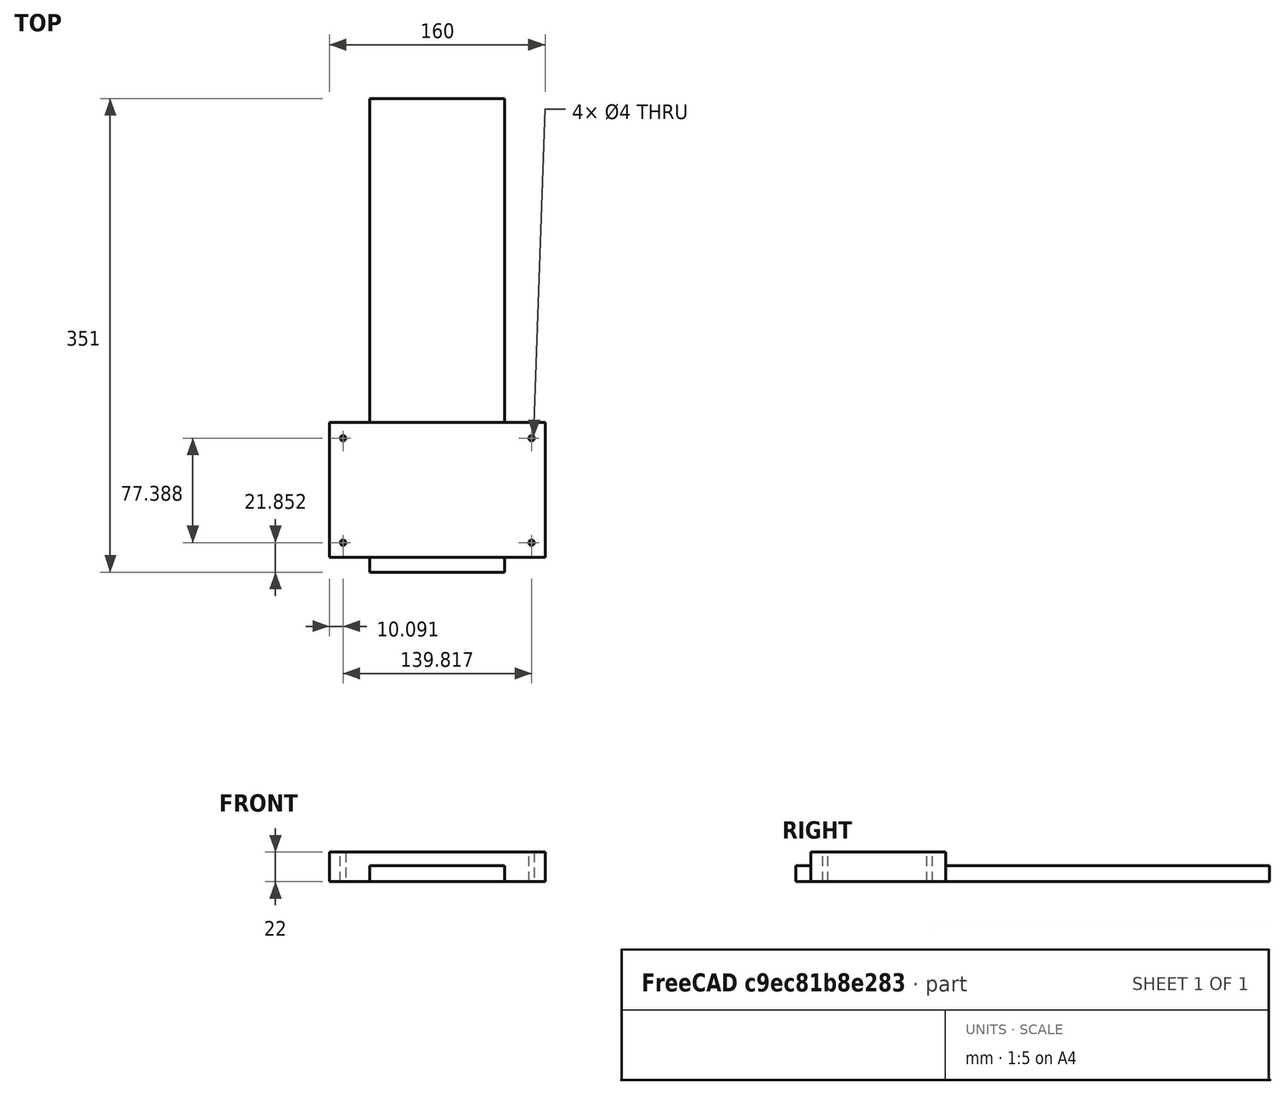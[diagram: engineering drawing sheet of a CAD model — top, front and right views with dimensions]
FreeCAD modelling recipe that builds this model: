
FCSTD DOCUMENT  (FreeCAD 0.20R29603 (Git))
Label: 100_Pedastil_Drawer
License: All rights reserved
LicenseURL: http://en.wikipedia.org/wiki/All_rights_reserved
objects: TechDraw::DrawViewDimension×6, Sketcher::SketchObject×3, TechDraw::DrawViewBalloon×3, PartDesign::Pad×2, TechDraw::DrawViewPart×2, Spreadsheet::Sheet×1, PartDesign::Pocket×1, PartDesign::Body×1, TechDraw::DrawSVGTemplate×1, TechDraw::DrawPage×1
note: 10 computed .brp shape members not serialized (recipe doc carries the construction recipe); baked Part::Feature solids carry a one-line shape summary decoded from their .brp

FEATURE [Spreadsheet::Sheet] Spreadsheet
  cells = B4=Drawer; C4=Value; D4=Nominal; E4=Var; F4=Description; G4=FILE
FEATURE [Sketcher::SketchObject] Sketch
  FullyConstrained = false
  MapMode = 5
  Support = -> [XY_Plane]
  sketch-geometry (14):
    g0: LineSegment StartX=-50 StartY=0 StartZ=0 EndX=-50 EndY=340 EndZ=0
    g1: LineSegment StartX=-50 StartY=340 StartZ=0 EndX=50 EndY=340 EndZ=0
    g2: LineSegment StartX=50 StartY=340 StartZ=0 EndX=50 EndY=0 EndZ=0
    g3: LineSegment StartX=50 StartY=100 StartZ=0 EndX=80 EndY=100 EndZ=0
    g4: LineSegment StartX=80 StartY=100 StartZ=0 EndX=80 EndY=0 EndZ=0
    g5: LineSegment StartX=80 StartY=0 StartZ=0 EndX=50 EndY=0 EndZ=0
    g6: LineSegment StartX=-50 StartY=100 StartZ=0 EndX=-80 EndY=100 EndZ=0
    g7: LineSegment StartX=-80 StartY=100 StartZ=0 EndX=-80 EndY=0 EndZ=0
    g8: LineSegment StartX=-80 StartY=0 StartZ=0 EndX=-50 EndY=0 EndZ=0
    g9: LineSegment StartX=-50 StartY=100 StartZ=0 EndX=-50 EndY=340 EndZ=0
    g10: LineSegment StartX=50 StartY=100 StartZ=0 EndX=50 EndY=340 EndZ=0
    g11: LineSegment StartX=50 StartY=0 StartZ=0 EndX=50 EndY=-11 EndZ=0
    g12: LineSegment StartX=50 StartY=-11 StartZ=0 EndX=-50 EndY=-11 EndZ=0
    g13: LineSegment StartX=-50 StartY=-11 StartZ=0 EndX=-50 EndY=0 EndZ=0
  constraints (38):
    c: PointOnObject(g0,g-1)
    c: Vertical(g0)
    c: Coincident(g1,g0)
    c: Horizontal(g1)
    c: Coincident(g2,g1)
    c: PointOnObject(g2,g-1)
    c: Vertical(g2)
    c: DistanceY(g2,g2) = 340
    c: DistanceX(g0,g2) = 100
    c: Coincident(g3,g4)
    c: Coincident(g4,g5)
    c: Horizontal(g3)
    c: Horizontal(g5)
    c: Vertical(g4)
    c: PointOnObject(g3,g2)
    c: PointOnObject(g4,g-1)
    c: Coincident(g6,g7)
    c: Coincident(g7,g8)
    c: Horizontal(g6)
    c: Horizontal(g8)
    c: Vertical(g7)
    c: PointOnObject(g6,g0)
    c: PointOnObject(g7,g-1)
    c: Equal(g4,g7)
    c: DistanceY(g4,g4) = 100
    c: DistanceX(g5,g5) = 30
    c: Equal(g5,g8)
    c: Coincident(g9,g6)
    c: Coincident(g9,g1)
    c: Coincident(g10,g3)
    c: Coincident(g10,g1)
    c: Coincident(g11,g12)
    c: Coincident(g12,g13)
    c: Horizontal(g12)
    c: Vertical(g11)
    c: Vertical(g13)
    c: DistanceY(g13,g13) = 11
    c: Coincident(g13,g8)
FEATURE [PartDesign::Pad] Pad
  Direction = (0,0,1)
  Length = 12
  Length2 = 10
  Profile = -> Sketch
  ReferenceAxis = -> Sketch [N_Axis]
  Type = 0
FEATURE [Sketcher::SketchObject] Sketch001
  ExternalGeometry = -> [Pad]
  FullyConstrained = true
  MapMode = 5
  Placement = pos=(0,0,12) rot=(0,0,1;0rad)
  Support = -> [Pad]
  sketch-geometry (4):
    g0: LineSegment StartX=-80 StartY=100 StartZ=0 EndX=80 EndY=100 EndZ=0
    g1: LineSegment StartX=80 StartY=100 StartZ=0 EndX=80 EndY=0 EndZ=0
    g2: LineSegment StartX=80 StartY=0 StartZ=0 EndX=-80 EndY=0 EndZ=0
    g3: LineSegment StartX=-80 StartY=0 StartZ=0 EndX=-80 EndY=100 EndZ=0
  constraints (10):
    c: Coincident(g0,g1)
    c: Coincident(g1,g2)
    c: Coincident(g2,g3)
    c: Coincident(g3,g0)
    c: Horizontal(g2)
    c: Vertical(g1)
    c: Vertical(g3)
    c: Coincident(g0,g-3)
    c: PointOnObject(g1,g-1)
    c: Coincident(g0,g-4)
FEATURE [PartDesign::Pad] Pad001
  BaseFeature = -> Pad
  Direction = (0,0,1)
  Length = 10
  Length2 = 10
  Profile = -> Sketch001
  ReferenceAxis = -> Sketch001 [N_Axis]
  Type = 0
FEATURE [Sketcher::SketchObject] Sketch002
  FullyConstrained = false
  MapMode = 5
  Placement = pos=(0,0,22) rot=(0,0,1;0rad)
  Support = -> [Pad001]
  sketch-geometry (9):
    g0: LineSegment StartX=-69.9086 StartY=88.2397 StartZ=0 EndX=69.9086 EndY=88.2397 EndZ=0
    g1: LineSegment StartX=69.9086 StartY=88.2397 StartZ=0 EndX=69.9086 EndY=10.8518 EndZ=0
    g2: LineSegment StartX=-69.9086 StartY=10.8518 StartZ=0 EndX=-69.9086 EndY=88.2397 EndZ=0
    g3: LineSegment StartX=-69.9086 StartY=10.8518 StartZ=0 EndX=0 EndY=10.8518 EndZ=0
    g4: LineSegment StartX=0 StartY=10.8518 StartZ=0 EndX=69.9086 EndY=10.8518 EndZ=0
    g5: Circle CenterX=-69.9086 CenterY=88.2397 CenterZ=0 NormalX=0 NormalY=0 NormalZ=1 AngleXU=0 Radius=2
    g6: Circle CenterX=69.9086 CenterY=88.2397 CenterZ=0 NormalX=0 NormalY=0 NormalZ=1 AngleXU=0 Radius=2
    g7: Circle CenterX=69.9086 CenterY=10.8518 CenterZ=0 NormalX=0 NormalY=0 NormalZ=1 AngleXU=0 Radius=2
    g8: Circle CenterX=-69.9086 CenterY=10.8518 CenterZ=0 NormalX=0 NormalY=0 NormalZ=1 AngleXU=0 Radius=2
  constraints (20):
    c: Coincident(g0,g1)
    c: Coincident(g2,g0)
    c: Horizontal(g0)
    c: Vertical(g1)
    c: Vertical(g2)
    c: Coincident(g3,g2)
    c: PointOnObject(g3,g-2)
    c: Horizontal(g3)
    c: Coincident(g4,g3)
    c: Coincident(g4,g1)
    c: Horizontal(g4)
    c: Equal(g4,g3)
    c: Coincident(g5,g0)
    c: Coincident(g6,g0)
    c: Coincident(g7,g1)
    c: Coincident(g8,g2)
    c: Equal(g8,g5)
    c: Equal(g5,g6)
    c: Equal(g6,g7)
    c: Diameter(g6) = 4
FEATURE [PartDesign::Pocket] Pocket
  BaseFeature = -> Pad001
  Direction = (0,0,-1)
  Length = 5
  Length2 = 5
  Profile = -> Sketch002
  ReferenceAxis = -> Sketch002 [N_Axis]
  Type = 1
FEATURE [PartDesign::Body] Body
  Group = -> [Sketch,Pad,Sketch001,Pad001,Sketch002,Pocket]
  Origin = -> Origin
  Tip = -> Pocket
FEATURE [TechDraw::DrawSVGTemplate] Template
  EditableTexts = Designed_by_Name=RIP; Drawing_number=100_Pedastil_Drawer; FC-Date=2023 04 01; FC-SC=0.5; FC-SH=1/1; FC-Title=Drawer Support; Subtitle=..; Weight=00
  Height = 210
  Orientation = 1
  Width = 297
FEATURE [TechDraw::DrawViewPart] View
  CoarseView = false
  Direction = (0,0,1)
  Focus = 100
  HardHidden = false
  IsoCount = 0
  IsoHidden = false
  IsoVisible = false
  LockPosition = false
  Perspective = false
  Rotation = 90
  Scale = 0.5
  ScaleType = 2
  SeamHidden = false
  SeamVisible = true
  SmoothHidden = false
  SmoothVisible = true
  Source = -> [Pocket,Template]
  X = 128.023
  XDirection = (0,0,1)
  Y = 142.617
FEATURE [TechDraw::DrawViewPart] View001
  CoarseView = false
  Direction = (1,0,0)
  Focus = 100
  HardHidden = false
  IsoCount = 0
  IsoHidden = false
  IsoVisible = false
  LockPosition = false
  Perspective = false
  Rotation = 0
  Scale = 0.5
  ScaleType = 2
  SeamHidden = false
  SeamVisible = true
  SmoothHidden = false
  SmoothVisible = true
  Source = -> [Template,Pocket]
  X = 127.304
  XDirection = (0,-1,0)
  Y = 77.5234
FEATURE [TechDraw::DrawViewDimension] Dimension
  AngleOverride = false
  Arbitrary = false
  ArbitraryTolerances = false
  EqualTolerance = true
  ExtensionAngle = 0
  FormatSpec = %.2w
  FormatSpecOverTolerance = %+.2w
  FormatSpecUnderTolerance = %+.2w
  Inverted = false
  LineAngle = 0
  LockPosition = false
  MeasureType = 1
  OverTolerance = 0
  References2D = -> [View]
  Rotation = 0
  ScaleType = 0
  TheoreticalExact = false
  Type = 1
  UnderTolerance = 0
  X = 2.09022
  Y = 50.4924
FEATURE [TechDraw::DrawViewDimension] Dimension001
  AngleOverride = false
  Arbitrary = false
  ArbitraryTolerances = false
  EqualTolerance = true
  ExtensionAngle = 0
  FormatSpec = %.2w
  FormatSpecOverTolerance = %+.2w
  FormatSpecUnderTolerance = %+.2w
  Inverted = false
  LineAngle = 0
  LockPosition = false
  MeasureType = 1
  OverTolerance = 0
  References2D = -> [View]
  Rotation = 0
  ScaleType = 0
  TheoreticalExact = false
  Type = 2
  UnderTolerance = 0
  X = -102.382
  Y = 4.29162
FEATURE [TechDraw::DrawViewDimension] Dimension002
  AngleOverride = false
  Arbitrary = false
  ArbitraryTolerances = false
  EqualTolerance = true
  ExtensionAngle = 0
  FormatSpec = %.2w
  FormatSpecOverTolerance = %+.2w
  FormatSpecUnderTolerance = %+.2w
  Inverted = false
  LineAngle = 0
  LockPosition = false
  MeasureType = 1
  OverTolerance = 0
  References2D = -> [View]
  Rotation = 0
  ScaleType = 0
  TheoreticalExact = false
  Type = 2
  UnderTolerance = 0
  X = 121.367
  Y = 2.2014
FEATURE [TechDraw::DrawViewDimension] Dimension003
  AngleOverride = false
  Arbitrary = false
  ArbitraryTolerances = false
  EqualTolerance = true
  ExtensionAngle = 0
  FormatSpec = %.2w
  FormatSpecOverTolerance = %+.2w
  FormatSpecUnderTolerance = %+.2w
  Inverted = false
  LineAngle = 0
  LockPosition = false
  MeasureType = 1
  OverTolerance = 0
  References2D = -> [View]
  Rotation = 0
  ScaleType = 0
  TheoreticalExact = false
  Type = 2
  UnderTolerance = 0
  X = 69.0604
  Y = 1.40978
FEATURE [TechDraw::DrawViewDimension] Dimension004
  AngleOverride = false
  Arbitrary = false
  ArbitraryTolerances = false
  EqualTolerance = true
  ExtensionAngle = 0
  FormatSpec = %.2w
  FormatSpecOverTolerance = %+.2w
  FormatSpecUnderTolerance = %+.2w
  Inverted = false
  LineAngle = 0
  LockPosition = false
  MeasureType = 1
  OverTolerance = 0
  References2D = -> [View001]
  Rotation = 0
  ScaleType = 0
  TheoreticalExact = false
  Type = 2
  UnderTolerance = 0
  X = -104.77
  Y = 17.5413
FEATURE [TechDraw::DrawViewDimension] Dimension005
  AngleOverride = false
  Arbitrary = false
  ArbitraryTolerances = false
  EqualTolerance = true
  ExtensionAngle = 0
  FormatSpec = %.2w
  FormatSpecOverTolerance = %+.2w
  FormatSpecUnderTolerance = %+.2w
  Inverted = false
  LineAngle = 0
  LockPosition = false
  MeasureType = 1
  OverTolerance = 0
  References2D = -> [View]
  Rotation = 0
  ScaleType = 0
  TheoreticalExact = false
  Type = 1
  UnderTolerance = 0
  X = 57.25
  Y = 53.5483
FEATURE [TechDraw::DrawViewBalloon] Balloon
  BubbleShape = 0
  EndType = 0
  EndTypeScale = 1
  KinkLength = 5
  LockPosition = false
  OriginX = -55.5
  OriginY = -50
  Rotation = 0
  ScaleType = 0
  ShapeScale = 1
  SourceView = -> View
  Text = 1
  TextWrapLen = -1
  X = 26.3044
  Y = -22.5413
FEATURE [TechDraw::DrawViewBalloon] Balloon001
  BubbleShape = 0
  EndType = 0
  EndTypeScale = 1
  KinkLength = 5
  LockPosition = false
  OriginX = 64.5
  OriginY = 2.3192e-12
  Rotation = 0
  ScaleType = 0
  ShapeScale = 1
  SourceView = -> View
  Text = 2
  TextWrapLen = -1
  X = 93.7503
  Y = -23.901
FEATURE [TechDraw::DrawViewBalloon] Balloon002
  BubbleShape = 0
  EndType = 0
  EndTypeScale = 1
  KinkLength = 5
  LockPosition = false
  OriginX = 164.5
  OriginY = 5
  Rotation = 0
  ScaleType = 0
  ShapeScale = 1
  SourceView = -> View001
  Text = 3
  TextWrapLen = -1
  X = 97.003
  Y = 80.2351
FEATURE [TechDraw::DrawPage] Page
  KeepUpdated = true
  NextBalloonIndex = 4
  ProjectionType = 0
  Template = -> Template
  Views = -> [View,View001,Dimension,Dimension001,Dimension002,Dimension003,Dimension004,Dimension005,Balloon,Balloon001,Balloon002]
